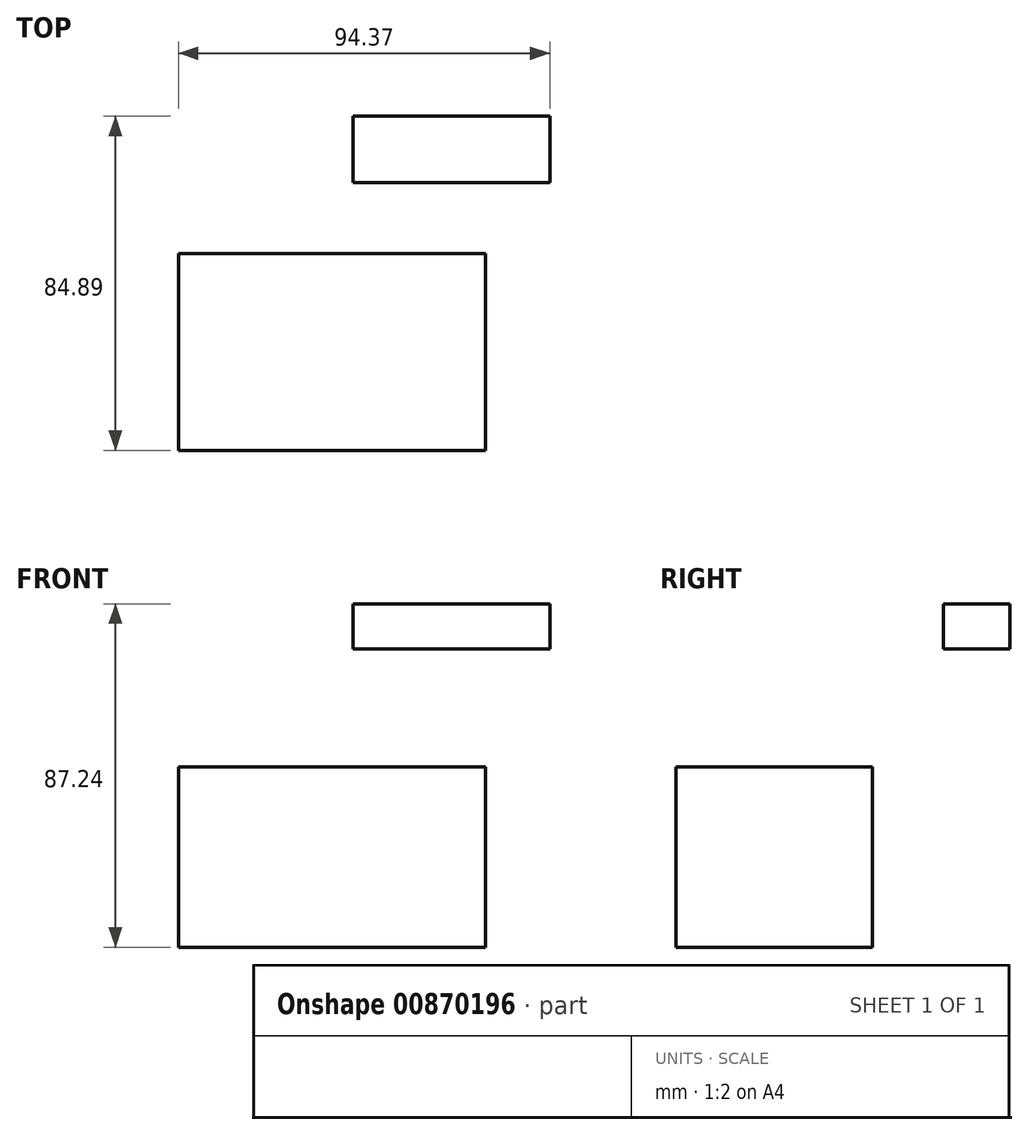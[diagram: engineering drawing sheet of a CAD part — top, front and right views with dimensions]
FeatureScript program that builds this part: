
annotation { "Feature Type Name" : "Feature", "Feature Type Description" : "" }
export const myFeature = defineFeature(function(context is Context, id is Id, definition is map)
    precondition{}
    {
        {
            var Q0;
            Q0=qCreatedBy(makeId("Right.planeOp"),FACE);
            var sketch = newSketch(context, id + "F0", { "sketchPlane" : qUnion([Q0])});
            skLineSegment(sketch, "E0.bottom", {"start": v(42.99, 52.54) * mm, "end": v(59.9, 52.54) * mm});
            skLineSegment(sketch, "E0.top", {"start": v(42.99, 64.03) * mm, "end": v(59.9, 64.03) * mm});
            skLineSegment(sketch, "E0.left", {"start": v(42.99, 52.54) * mm, "end": v(42.99, 64.03) * mm});
            skLineSegment(sketch, "E0.right", {"start": v(59.9, 52.54) * mm, "end": v(59.9, 64.03) * mm});
            skSolve(sketch);
        }
        {
            var Q0;
            Q0=qCreatedBy(makeId("Front.planeOp"),FACE);
            var sketch = newSketch(context, id + "F1", { "sketchPlane" : qUnion([Q0])});
            skLineSegment(sketch, "E1.bottom", {"start": v(-69.37, -23.2) * mm, "end": v(8.7, -23.2) * mm});
            skLineSegment(sketch, "E1.top", {"start": v(-69.37, 22.66) * mm, "end": v(8.7, 22.66) * mm});
            skLineSegment(sketch, "E1.left", {"start": v(-69.37, -23.2) * mm, "end": v(-69.37, 22.66) * mm});
            skLineSegment(sketch, "E1.right", {"start": v(8.7, -23.2) * mm, "end": v(8.7, 22.66) * mm});
            skSolve(sketch);
        }
        {
            var Q0;
            Q0=makeQuery(id+"F1.imprint","IMPRINT",FACE,{"disambiguationData":[TD([[makeQuery(id+"F1.imprint","IMPRINT",EDGE,{"derivedFrom":sQuery(id+"F1.wireOp",EDGE,"E1.bottom")}),1.0]])]});
            extrude(context, id + "F2", {"entities" : qUnion([Q0]), "depth" : 25 * mm, "offsetDistance" : 25 * mm, "hasSecondDirection" : true, "secondDirectionOppositeDirection" : true, "secondDirectionDepth" : 25 * mm});
        }
        {
            var Q0;
            Q0=makeQuery(id+"F0.imprint","IMPRINT",FACE,{"disambiguationData":[TD([[makeQuery(id+"F0.imprint","IMPRINT",EDGE,{"derivedFrom":sQuery(id+"F0.wireOp",EDGE,"E0.bottom")}),1.0]])]});
            extrude(context, id + "F3", {"entities" : qUnion([Q0]), "depth" : 25 * mm, "offsetDistance" : 25 * mm, "hasSecondDirection" : true, "secondDirectionOppositeDirection" : true, "secondDirectionDepth" : 25 * mm});
        }
    });
